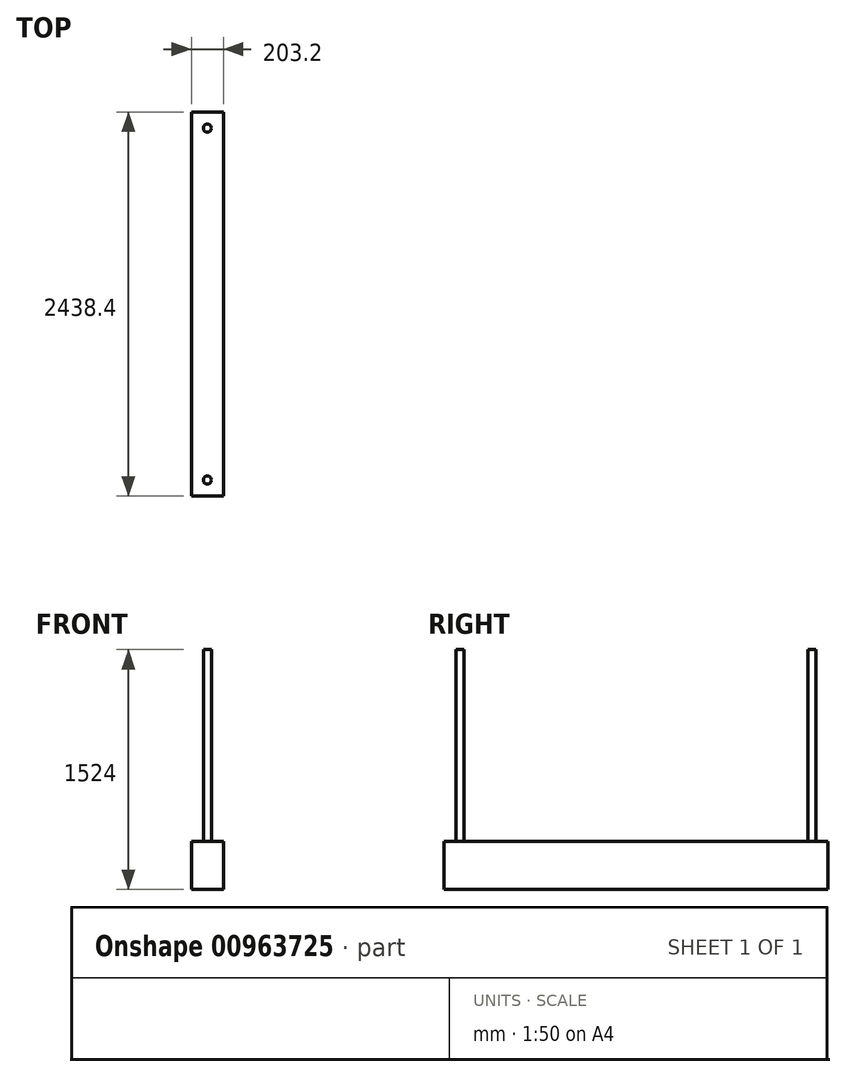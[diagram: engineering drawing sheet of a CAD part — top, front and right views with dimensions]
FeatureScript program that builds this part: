
annotation { "Feature Type Name" : "Feature", "Feature Type Description" : "" }
export const myFeature = defineFeature(function(context is Context, id is Id, definition is map)
    precondition{}
    {
        {
            var Q0;
            Q0=qCreatedBy(makeId("Top.planeOp"),FACE);
            var sketch = newSketch(context, id + "F0", { "sketchPlane" : qUnion([Q0])});
            skLineSegment(sketch, "E0", {"start": v(122.18, -1741.2) * mm, "end": v(325.38, -1741.2) * mm});
            skLineSegment(sketch, "E1", {"start": v(325.38, -1741.2) * mm, "end": v(325.38, 697.2) * mm});
            skLineSegment(sketch, "E2", {"start": v(325.38, 697.2) * mm, "end": v(122.18, 697.2) * mm});
            skLineSegment(sketch, "E3", {"start": v(122.18, 697.2) * mm, "end": v(122.18, -1741.2) * mm});
            skSolve(sketch);
        }
        {
            var Q0;
            Q0=makeQuery(id+"F0.imprint","IMPRINT",FACE,{"disambiguationData":[TD([[makeQuery(id+"F0.imprint","IMPRINT",EDGE,{"derivedFrom":sQuery(id+"F0.wireOp",EDGE,"E0")}),1.0]])]});
            extrude(context, id + "F1", {"entities" : qUnion([Q0]), "depth" : 304.8 * mm, "offsetDistance" : 25.4 * mm});
        }
        {
            var Q0;
            Q0=makeQuery(id+"F1.opExtrude","CAP_FACE",FACE,{"disambiguationData":[OSD([sQuery(id+"F0.wireOp",EDGE,"E0"),sQuery(id+"F0.wireOp",EDGE,"E1"),sQuery(id+"F0.wireOp",EDGE,"E2"),sQuery(id+"F0.wireOp",EDGE,"zbvfCdZV-5rQB-4tka-iKzs-aoV9D7Pk8jba"),sQuery(id+"F0.wireOp",EDGE,"CBg0Odci-znIz-hHVI-ncM7-tL2d96odwMIc"),sQuery(id+"F0.wireOp",EDGE,"E3")])],"isStart":false});
            var sketch = newSketch(context, id + "F2", { "sketchPlane" : qUnion([Q0])});
            skCircle(sketch, "E4", {"center": v(223.78, 595.6) * mm, "radius": 25.4 * mm});
            skCircle(sketch, "E5", {"center": v(223.78, -1639.6) * mm, "radius": 25.4 * mm});
            skSolve(sketch);
        }
        {
            var Q0;
            Q0=makeQuery(id+"F2.imprint","IMPRINT",FACE,{"disambiguationData":[TD([[makeQuery(id+"F2.imprint","IMPRINT",EDGE,{"derivedFrom":sQuery(id+"F2.wireOp",EDGE,"E5")}),1.0]])]});
            var Q1;
            Q1=makeQuery(id+"F2.imprint","IMPRINT",FACE,{"disambiguationData":[TD([[makeQuery(id+"F2.imprint","IMPRINT",EDGE,{"derivedFrom":sQuery(id+"F2.wireOp",EDGE,"E4")}),1.0]])]});
            var Q2;
            Q2=sQuery(id+"F2.wireOp",EDGE,"E5");
            var Q3;
            Q3=sQuery(id+"F2.wireOp",EDGE,"E4");
            extrude(context, id + "F3", {"entities" : qUnion([Q0, Q1]), "operationType" : NewBodyOperationType.ADD, "surfaceOperationType" : NewSurfaceOperationType.ADD, "surfaceEntities" : qUnion([Q2, Q3]), "depth" : 1219.2 * mm, "offsetDistance" : 25.4 * mm});
        }
    });
